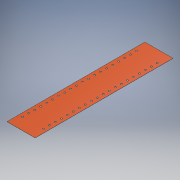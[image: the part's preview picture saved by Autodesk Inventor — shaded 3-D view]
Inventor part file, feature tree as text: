
AUTODESK INVENTOR PART (.ipt)
format: ipt  version: 2019 (Build 230136000, 136)  size: 191,488 bytes
history: native  units: mm
features: extrude x2, other x2, mirror x1
ambient origin geometry x8: Origin, YZ Plane, XZ Plane, XY Plane, X Axis, Y Axis, Z Axis, Center Point
bodies: Body1 (feature_tree)
feature tree (5):
  extrude  "Skin Body"  Depth=928.0mm
  extrude  "End Cut"  Depth=464.0mm
  mirror  "End Cut Mirror"
  other  "Skin Scheme"
  other  "End Cut Outline"
